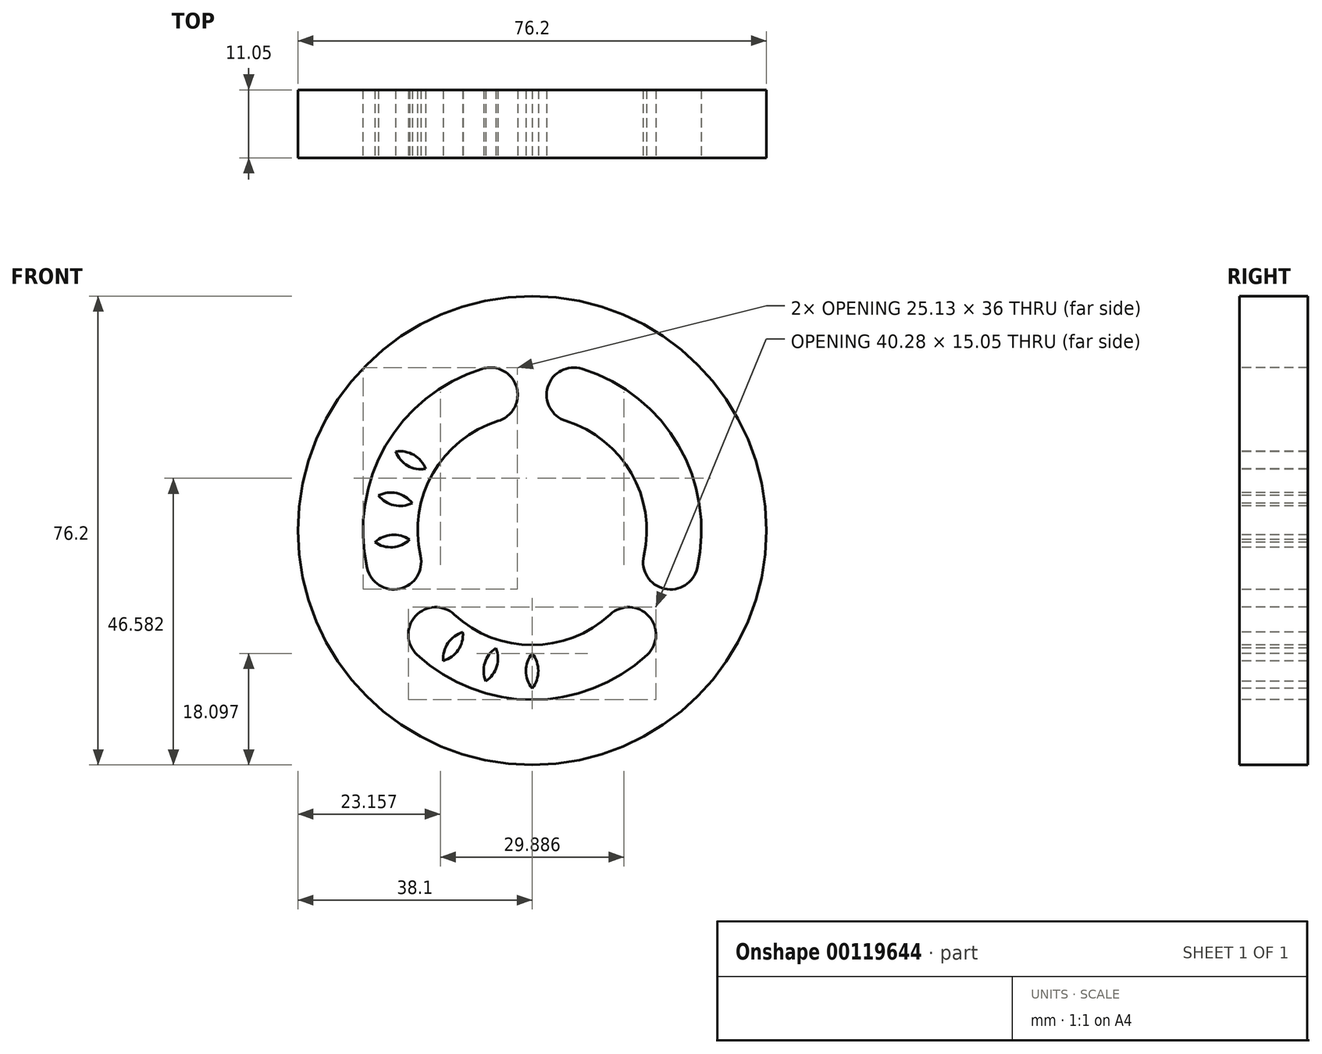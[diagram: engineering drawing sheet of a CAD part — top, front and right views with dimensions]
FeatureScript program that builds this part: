
annotation { "Feature Type Name" : "Feature", "Feature Type Description" : "" }
export const myFeature = defineFeature(function(context is Context, id is Id, definition is map)
    precondition{}
    {
        {
            var Q0;
            Q0=qCreatedBy(makeId("Front.planeOp"),FACE);
            var sketch = newSketch(context, id + "F0", { "sketchPlane" : qUnion([Q0])});
            skCircle(sketch, "E0", {"center": v(0, 0) * mm, "radius": 38.1 * mm});
            skSolve(sketch);
        }
        {
            var Q0;
            Q0 = qSketchRegion(id + "F0", true);
            extrude(context, id + "F1", {"entities" : qUnion([Q0]), "depth" : 11.05 * mm});
        }
        {
            var Q0;
            Q0=makeQuery(id+"F1.opExtrude","CAP_FACE",FACE,{"disambiguationData":[OSD([sQuery(id+"F0.wireOp",EDGE,"E0")])],"isStart":false});
            var sketch = newSketch(context, id + "F2", { "sketchPlane" : qUnion([Q0])});
            skCircle(sketch, "E1", {"center": v(0, 0) * mm, "radius": 7.94 * mm});
            skCircle(sketch, "E2", {"center": v(0, 0) * mm, "radius": 17.46 * mm});
            skCircle(sketch, "E3", {"center": v(0, 0) * mm, "radius": 28.7 * mm});
            skCircle(sketch, "E4", {"center": v(0, 23.08) * mm, "radius": 4.45 * mm, "construction": true});
            skLineSegment(sketch, "E5", {"start": v(0, 17.46) * mm, "end": v(0, 18.64) * mm, "construction": true});
            skLineSegment(sketch, "E6", {"start": v(0, 27.53) * mm, "end": v(0, 28.7) * mm, "construction": true});
            skCircle(sketch, "E7.1.0", {"center": v(-6.8, 22.06) * mm, "radius": 4.45 * mm});
            skCircle(sketch, "E7.2.0", {"center": v(-13, 19.07) * mm, "radius": 4.45 * mm});
            skCircle(sketch, "E7.3.0", {"center": v(-18.05, 14.4) * mm, "radius": 4.45 * mm});
            skCircle(sketch, "E7.4.0", {"center": v(-21.49, 8.43) * mm, "radius": 4.45 * mm});
            skCircle(sketch, "E7.5.0", {"center": v(-23.02, 1.72) * mm, "radius": 4.45 * mm});
            skCircle(sketch, "E7.6.0", {"center": v(-22.5, -5.14) * mm, "radius": 4.45 * mm});
            skCircle(sketch, "E7.7.0", {"center": v(-19.99, -11.54) * mm, "radius": 4.45 * mm, "construction": true});
            skCircle(sketch, "E7.8.0", {"center": v(-15.7, -16.92) * mm, "radius": 4.45 * mm});
            skCircle(sketch, "E7.9.0", {"center": v(-10.02, -20.8) * mm, "radius": 4.45 * mm});
            skCircle(sketch, "E7.10.0", {"center": v(-3.44, -22.82) * mm, "radius": 4.45 * mm});
            skCircle(sketch, "E7.11.0", {"center": v(3.44, -22.82) * mm, "radius": 4.45 * mm});
            skCircle(sketch, "E7.12.0", {"center": v(10.02, -20.8) * mm, "radius": 4.45 * mm});
            skCircle(sketch, "E7.13.0", {"center": v(15.7, -16.92) * mm, "radius": 4.45 * mm});
            skCircle(sketch, "E7.14.0", {"center": v(19.99, -11.54) * mm, "radius": 4.45 * mm, "construction": true});
            skCircle(sketch, "E7.15.0", {"center": v(22.5, -5.14) * mm, "radius": 4.45 * mm});
            skCircle(sketch, "E7.16.0", {"center": v(23.02, 1.72) * mm, "radius": 4.45 * mm});
            skCircle(sketch, "E7.17.0", {"center": v(21.49, 8.43) * mm, "radius": 4.45 * mm});
            skCircle(sketch, "E8.1.18.0", {"center": v(18.05, 14.4) * mm, "radius": 4.45 * mm});
            skCircle(sketch, "E8.1.19.0", {"center": v(13, 19.07) * mm, "radius": 4.45 * mm});
            skCircle(sketch, "E8.1.20.0", {"center": v(6.8, 22.06) * mm, "radius": 4.45 * mm});
            skArc(sketch, "E9", {"start": v(26.84, -6.13) * mm, "mid": v(23.84, 13.76) * mm, "end": v(8.11, 26.3) * mm});
            skArc(sketch, "E10", {"start": v(5.5, 17.8) * mm, "mid": v(16.14, 9.32) * mm, "end": v(18.17, -4.15) * mm});
            skArc(sketch, "E11", {"start": v(18.72, -20.18) * mm, "mid": v(0, -27.53) * mm, "end": v(-18.72, -20.18) * mm});
            skArc(sketch, "E12", {"start": v(-8.11, 26.3) * mm, "mid": v(-23.84, 13.76) * mm, "end": v(-26.84, -6.13) * mm});
            skArc(sketch, "E13", {"start": v(-5.5, 17.8) * mm, "mid": v(-16.14, 9.32) * mm, "end": v(-18.17, -4.15) * mm});
            skArc(sketch, "E14", {"start": v(-12.68, -13.66) * mm, "mid": v(0, -18.64) * mm, "end": v(12.68, -13.66) * mm});
            skSolve(sketch);
        }
        {
            var Q0;
            {var subQ0=sQuery(id+"F2.wireOp",EDGE,"E7.6.0");var subQ1=sQuery(id+"F2.wireOp",EDGE,"E7.5.0");var subQ2=makeQuery(id+"F2.imprint","INTERSECT",VERTEX,{"disambiguationData":[OD(0.0)],"derivedFrom":[subQ1,subQ0]});Q0=makeQuery(id+"F2.imprint","IMPRINT",FACE,{"disambiguationData":[TD([[makeQuery(id+"F2.imprint","IMPRINT",EDGE,{"disambiguationData":[TD([[subQ2,-1.0]])],"derivedFrom":subQ1}),-1.0]])]});}
            var Q1;
            {var subQ0=sQuery(id+"F2.wireOp",EDGE,"E12");var subQ1=sQuery(id+"F2.wireOp",EDGE,"E7.5.0");var subQ2=makeQuery(id+"F2.imprint","INTERSECT",VERTEX,{"derivedFrom":[subQ1,subQ0]});Q1=makeQuery(id+"F2.imprint","IMPRINT",FACE,{"disambiguationData":[TD([[makeQuery(id+"F2.imprint","IMPRINT",EDGE,{"disambiguationData":[TD([[subQ2,-1.0]])],"derivedFrom":subQ1}),-1.0]])]});}
            var Q2;
            {var subQ0=sQuery(id+"F2.wireOp",EDGE,"E7.6.0");var subQ1=sQuery(id+"F2.wireOp",EDGE,"E7.5.0");var subQ2=makeQuery(id+"F2.imprint","INTERSECT",VERTEX,{"disambiguationData":[OD(0.0)],"derivedFrom":[subQ1,subQ0]});Q2=makeQuery(id+"F2.imprint","IMPRINT",FACE,{"disambiguationData":[TD([[makeQuery(id+"F2.imprint","IMPRINT",EDGE,{"disambiguationData":[TD([[subQ2,-1.0]])],"derivedFrom":subQ1}),1.0]])]});}
            var Q3;
            {var subQ0=sQuery(id+"F2.wireOp",EDGE,"E7.6.0");var subQ1=sQuery(id+"F2.wireOp",EDGE,"E7.5.0");var subQ2=makeQuery(id+"F2.imprint","INTERSECT",VERTEX,{"disambiguationData":[OD(1.0)],"derivedFrom":[subQ1,subQ0]});Q3=makeQuery(id+"F2.imprint","IMPRINT",FACE,{"disambiguationData":[TD([[makeQuery(id+"F2.imprint","IMPRINT",EDGE,{"disambiguationData":[TD([[subQ2,-1.0]])],"derivedFrom":subQ1}),-1.0]])]});}
            var Q4;
            {var subQ1=sQuery(id+"F2.wireOp",EDGE,"E7.5.0");var subQ6=sQuery(id+"F2.wireOp",EDGE,"E7.4.0");var subQ7=makeQuery(id+"F2.imprint","INTERSECT",VERTEX,{"disambiguationData":[OD(0.0)],"derivedFrom":[subQ6,subQ1]});Q4=makeQuery(id+"F2.imprint","IMPRINT",FACE,{"disambiguationData":[TD([[makeQuery(id+"F2.imprint","IMPRINT",EDGE,{"disambiguationData":[TD([[subQ7,-1.0]])],"derivedFrom":subQ6}),-1.0]])]});}
            var Q5;
            {var subQ0=sQuery(id+"F2.wireOp",EDGE,"E7.5.0");var subQ1=sQuery(id+"F2.wireOp",EDGE,"E7.4.0");var subQ2=makeQuery(id+"F2.imprint","INTERSECT",VERTEX,{"disambiguationData":[OD(1.0)],"derivedFrom":[subQ1,subQ0]});Q5=makeQuery(id+"F2.imprint","IMPRINT",FACE,{"disambiguationData":[TD([[makeQuery(id+"F2.imprint","IMPRINT",EDGE,{"disambiguationData":[TD([[subQ2,-1.0]])],"derivedFrom":subQ1}),-1.0]])]});}
            var Q6;
            {var subQ0=sQuery(id+"F2.wireOp",EDGE,"E7.4.0");var subQ1=sQuery(id+"F2.wireOp",EDGE,"E7.3.0");var subQ2=makeQuery(id+"F2.imprint","INTERSECT",VERTEX,{"disambiguationData":[OD(1.0)],"derivedFrom":[subQ1,subQ0]});Q6=makeQuery(id+"F2.imprint","IMPRINT",FACE,{"disambiguationData":[TD([[makeQuery(id+"F2.imprint","IMPRINT",EDGE,{"disambiguationData":[TD([[subQ2,-1.0]])],"derivedFrom":subQ1}),-1.0]])]});}
            var Q7;
            {var subQ0=sQuery(id+"F2.wireOp",EDGE,"E7.3.0");var subQ1=sQuery(id+"F2.wireOp",EDGE,"E7.2.0");var subQ2=makeQuery(id+"F2.imprint","INTERSECT",VERTEX,{"disambiguationData":[OD(1.0)],"derivedFrom":[subQ1,subQ0]});Q7=makeQuery(id+"F2.imprint","IMPRINT",FACE,{"disambiguationData":[TD([[makeQuery(id+"F2.imprint","IMPRINT",EDGE,{"disambiguationData":[TD([[subQ2,-1.0]])],"derivedFrom":subQ1}),-1.0]])]});}
            var Q8;
            {var subQ0=sQuery(id+"F2.wireOp",EDGE,"E13");var subQ1=sQuery(id+"F2.wireOp",EDGE,"E7.1.0");var subQ2=makeQuery(id+"F2.imprint","INTERSECT",VERTEX,{"derivedFrom":[subQ1,subQ0]});Q8=makeQuery(id+"F2.imprint","IMPRINT",FACE,{"disambiguationData":[TD([[makeQuery(id+"F2.imprint","IMPRINT",EDGE,{"disambiguationData":[TD([[subQ2,1.0]])],"derivedFrom":subQ1}),-1.0]])]});}
            var Q9;
            {var subQ0=sQuery(id+"F2.wireOp",EDGE,"E7.1.0");var subQ1=makeQuery(id+"F2.imprint","INTERSECT",VERTEX,{"derivedFrom":[subQ0,sQuery(id+"F2.wireOp",EDGE,"E12")]});Q9=makeQuery(id+"F2.imprint","IMPRINT",FACE,{"disambiguationData":[TD([[makeQuery(id+"F2.imprint","IMPRINT",EDGE,{"disambiguationData":[TD([[subQ1,-1.0]])],"derivedFrom":subQ0}),1.0]])]});}
            var Q10;
            {var subQ1=sQuery(id+"F2.wireOp",EDGE,"E7.2.0");var subQ4=sQuery(id+"F2.wireOp",EDGE,"E7.1.0");var subQ5=makeQuery(id+"F2.imprint","INTERSECT",VERTEX,{"disambiguationData":[OD(0.0)],"derivedFrom":[subQ4,subQ1]});Q10=makeQuery(id+"F2.imprint","IMPRINT",FACE,{"disambiguationData":[TD([[makeQuery(id+"F2.imprint","IMPRINT",EDGE,{"disambiguationData":[TD([[subQ5,-1.0]])],"derivedFrom":subQ4}),-1.0]])]});}
            var Q11;
            {var subQ0=sQuery(id+"F2.wireOp",EDGE,"E7.2.0");var subQ1=sQuery(id+"F2.wireOp",EDGE,"E7.1.0");var subQ2=makeQuery(id+"F2.imprint","INTERSECT",VERTEX,{"disambiguationData":[OD(0.0)],"derivedFrom":[subQ1,subQ0]});Q11=makeQuery(id+"F2.imprint","IMPRINT",FACE,{"disambiguationData":[TD([[makeQuery(id+"F2.imprint","IMPRINT",EDGE,{"disambiguationData":[TD([[subQ2,-1.0]])],"derivedFrom":subQ1}),1.0]])]});}
            var Q12;
            {var subQ0=sQuery(id+"F2.wireOp",EDGE,"E12");var subQ1=sQuery(id+"F2.wireOp",EDGE,"E7.1.0");var subQ2=makeQuery(id+"F2.imprint","INTERSECT",VERTEX,{"derivedFrom":[subQ1,subQ0]});Q12=makeQuery(id+"F2.imprint","IMPRINT",FACE,{"disambiguationData":[TD([[makeQuery(id+"F2.imprint","IMPRINT",EDGE,{"disambiguationData":[TD([[subQ2,-1.0]])],"derivedFrom":subQ1}),-1.0]])]});}
            var Q13;
            {var subQ0=sQuery(id+"F2.wireOp",EDGE,"E12");var subQ1=sQuery(id+"F2.wireOp",EDGE,"E7.2.0");var subQ2=makeQuery(id+"F2.imprint","INTERSECT",VERTEX,{"derivedFrom":[subQ1,subQ0]});Q13=makeQuery(id+"F2.imprint","IMPRINT",FACE,{"disambiguationData":[TD([[makeQuery(id+"F2.imprint","IMPRINT",EDGE,{"disambiguationData":[TD([[subQ2,-1.0]])],"derivedFrom":subQ1}),-1.0]])]});}
            var Q14;
            {var subQ0=sQuery(id+"F2.wireOp",EDGE,"E7.3.0");var subQ1=sQuery(id+"F2.wireOp",EDGE,"E7.2.0");var subQ2=makeQuery(id+"F2.imprint","INTERSECT",VERTEX,{"disambiguationData":[OD(0.0)],"derivedFrom":[subQ1,subQ0]});Q14=makeQuery(id+"F2.imprint","IMPRINT",FACE,{"disambiguationData":[TD([[makeQuery(id+"F2.imprint","IMPRINT",EDGE,{"disambiguationData":[TD([[subQ2,-1.0]])],"derivedFrom":subQ1}),1.0]])]});}
            var Q15;
            {var subQ0=sQuery(id+"F2.wireOp",EDGE,"E7.3.0");var subQ4=sQuery(id+"F2.wireOp",EDGE,"E7.2.0");var subQ5=makeQuery(id+"F2.imprint","INTERSECT",VERTEX,{"disambiguationData":[OD(0.0)],"derivedFrom":[subQ4,subQ0]});Q15=makeQuery(id+"F2.imprint","IMPRINT",FACE,{"disambiguationData":[TD([[makeQuery(id+"F2.imprint","IMPRINT",EDGE,{"disambiguationData":[TD([[subQ5,-1.0]])],"derivedFrom":subQ4}),-1.0]])]});}
            var Q16;
            {var subQ0=sQuery(id+"F2.wireOp",EDGE,"E7.4.0");var subQ1=sQuery(id+"F2.wireOp",EDGE,"E7.3.0");var subQ2=makeQuery(id+"F2.imprint","INTERSECT",VERTEX,{"disambiguationData":[OD(0.0)],"derivedFrom":[subQ1,subQ0]});Q16=makeQuery(id+"F2.imprint","IMPRINT",FACE,{"disambiguationData":[TD([[makeQuery(id+"F2.imprint","IMPRINT",EDGE,{"disambiguationData":[TD([[subQ2,-1.0]])],"derivedFrom":subQ1}),-1.0]])]});}
            var Q17;
            {var subQ0=sQuery(id+"F2.wireOp",EDGE,"E7.4.0");var subQ1=sQuery(id+"F2.wireOp",EDGE,"E7.3.0");var subQ2=makeQuery(id+"F2.imprint","INTERSECT",VERTEX,{"disambiguationData":[OD(0.0)],"derivedFrom":[subQ1,subQ0]});Q17=makeQuery(id+"F2.imprint","IMPRINT",FACE,{"disambiguationData":[TD([[makeQuery(id+"F2.imprint","IMPRINT",EDGE,{"disambiguationData":[TD([[subQ2,-1.0]])],"derivedFrom":subQ1}),1.0]])]});}
            var Q18;
            {var subQ0=sQuery(id+"F2.wireOp",EDGE,"E12");var subQ1=sQuery(id+"F2.wireOp",EDGE,"E7.4.0");var subQ2=makeQuery(id+"F2.imprint","INTERSECT",VERTEX,{"derivedFrom":[subQ1,subQ0]});Q18=makeQuery(id+"F2.imprint","IMPRINT",FACE,{"disambiguationData":[TD([[makeQuery(id+"F2.imprint","IMPRINT",EDGE,{"disambiguationData":[TD([[subQ2,-1.0]])],"derivedFrom":subQ1}),-1.0]])]});}
            var Q19;
            {var subQ0=sQuery(id+"F2.wireOp",EDGE,"E7.5.0");var subQ1=sQuery(id+"F2.wireOp",EDGE,"E7.4.0");var subQ2=makeQuery(id+"F2.imprint","INTERSECT",VERTEX,{"disambiguationData":[OD(0.0)],"derivedFrom":[subQ1,subQ0]});Q19=makeQuery(id+"F2.imprint","IMPRINT",FACE,{"disambiguationData":[TD([[makeQuery(id+"F2.imprint","IMPRINT",EDGE,{"disambiguationData":[TD([[subQ2,-1.0]])],"derivedFrom":subQ1}),1.0]])]});}
            var Q20;
            {var subQ0=sQuery(id+"F2.wireOp",EDGE,"E12");var subQ1=sQuery(id+"F2.wireOp",EDGE,"E7.3.0");var subQ2=makeQuery(id+"F2.imprint","INTERSECT",VERTEX,{"derivedFrom":[subQ1,subQ0]});Q20=makeQuery(id+"F2.imprint","IMPRINT",FACE,{"disambiguationData":[TD([[makeQuery(id+"F2.imprint","IMPRINT",EDGE,{"disambiguationData":[TD([[subQ2,-1.0]])],"derivedFrom":subQ1}),-1.0]])]});}
            var Q21;
            {var subQ0=sQuery(id+"F2.wireOp",EDGE,"E8.1.20.0");var subQ1=sQuery(id+"F2.wireOp",EDGE,"E8.1.19.0");var subQ2=makeQuery(id+"F2.imprint","INTERSECT",VERTEX,{"disambiguationData":[OD(0.0)],"derivedFrom":[subQ1,subQ0]});Q21=makeQuery(id+"F2.imprint","IMPRINT",FACE,{"disambiguationData":[TD([[makeQuery(id+"F2.imprint","IMPRINT",EDGE,{"disambiguationData":[TD([[subQ2,-1.0]])],"derivedFrom":subQ1}),-1.0]])]});}
            var Q22;
            {var subQ0=sQuery(id+"F2.wireOp",EDGE,"E9");var subQ1=sQuery(id+"F2.wireOp",EDGE,"E8.1.19.0");var subQ2=makeQuery(id+"F2.imprint","INTERSECT",VERTEX,{"derivedFrom":[subQ1,subQ0]});Q22=makeQuery(id+"F2.imprint","IMPRINT",FACE,{"disambiguationData":[TD([[makeQuery(id+"F2.imprint","IMPRINT",EDGE,{"disambiguationData":[TD([[subQ2,-1.0]])],"derivedFrom":subQ1}),-1.0]])]});}
            var Q23;
            {var subQ1=sQuery(id+"F2.wireOp",EDGE,"E8.1.19.0");var subQ6=sQuery(id+"F2.wireOp",EDGE,"E8.1.18.0");var subQ8=makeQuery(id+"F2.imprint","INTERSECT",VERTEX,{"disambiguationData":[OD(0.0)],"derivedFrom":[subQ6,subQ1]});Q23=makeQuery(id+"F2.imprint","IMPRINT",FACE,{"disambiguationData":[TD([[makeQuery(id+"F2.imprint","IMPRINT",EDGE,{"disambiguationData":[TD([[subQ8,-1.0]])],"derivedFrom":subQ6}),-1.0]])]});}
            var Q24;
            {var subQ0=sQuery(id+"F2.wireOp",EDGE,"E8.1.20.0");var subQ1=sQuery(id+"F2.wireOp",EDGE,"E8.1.19.0");var subQ2=makeQuery(id+"F2.imprint","INTERSECT",VERTEX,{"disambiguationData":[OD(0.0)],"derivedFrom":[subQ1,subQ0]});Q24=makeQuery(id+"F2.imprint","IMPRINT",FACE,{"disambiguationData":[TD([[makeQuery(id+"F2.imprint","IMPRINT",EDGE,{"disambiguationData":[TD([[subQ2,-1.0]])],"derivedFrom":subQ1}),1.0]])]});}
            var Q25;
            {var subQ0=sQuery(id+"F2.wireOp",EDGE,"E8.1.20.0");var subQ1=sQuery(id+"F2.wireOp",EDGE,"E8.1.19.0");var subQ2=makeQuery(id+"F2.imprint","INTERSECT",VERTEX,{"disambiguationData":[OD(1.0)],"derivedFrom":[subQ1,subQ0]});Q25=makeQuery(id+"F2.imprint","IMPRINT",FACE,{"disambiguationData":[TD([[makeQuery(id+"F2.imprint","IMPRINT",EDGE,{"disambiguationData":[TD([[subQ2,-1.0]])],"derivedFrom":subQ1}),-1.0]])]});}
            var Q26;
            {var subQ0=sQuery(id+"F2.wireOp",EDGE,"E9");var subQ1=sQuery(id+"F2.wireOp",EDGE,"E8.1.18.0");var subQ2=makeQuery(id+"F2.imprint","INTERSECT",VERTEX,{"derivedFrom":[subQ1,subQ0]});Q26=makeQuery(id+"F2.imprint","IMPRINT",FACE,{"disambiguationData":[TD([[makeQuery(id+"F2.imprint","IMPRINT",EDGE,{"disambiguationData":[TD([[subQ2,-1.0]])],"derivedFrom":subQ1}),-1.0]])]});}
            var Q27;
            {var subQ0=sQuery(id+"F2.wireOp",EDGE,"E8.1.19.0");var subQ1=sQuery(id+"F2.wireOp",EDGE,"E8.1.18.0");var subQ2=makeQuery(id+"F2.imprint","INTERSECT",VERTEX,{"disambiguationData":[OD(1.0)],"derivedFrom":[subQ1,subQ0]});Q27=makeQuery(id+"F2.imprint","IMPRINT",FACE,{"disambiguationData":[TD([[makeQuery(id+"F2.imprint","IMPRINT",EDGE,{"disambiguationData":[TD([[subQ2,-1.0]])],"derivedFrom":subQ1}),-1.0]])]});}
            var Q28;
            {var subQ0=sQuery(id+"F2.wireOp",EDGE,"E8.1.19.0");var subQ1=sQuery(id+"F2.wireOp",EDGE,"E8.1.18.0");var subQ2=makeQuery(id+"F2.imprint","INTERSECT",VERTEX,{"disambiguationData":[OD(0.0)],"derivedFrom":[subQ1,subQ0]});Q28=makeQuery(id+"F2.imprint","IMPRINT",FACE,{"disambiguationData":[TD([[makeQuery(id+"F2.imprint","IMPRINT",EDGE,{"disambiguationData":[TD([[subQ2,-1.0]])],"derivedFrom":subQ1}),1.0]])]});}
            var Q29;
            {var subQ1=sQuery(id+"F2.wireOp",EDGE,"E8.1.18.0");var subQ4=sQuery(id+"F2.wireOp",EDGE,"E7.17.0");var subQ5=makeQuery(id+"F2.imprint","INTERSECT",VERTEX,{"disambiguationData":[OD(0.0)],"derivedFrom":[subQ4,subQ1]});Q29=makeQuery(id+"F2.imprint","IMPRINT",FACE,{"disambiguationData":[TD([[makeQuery(id+"F2.imprint","IMPRINT",EDGE,{"disambiguationData":[TD([[subQ5,-1.0]])],"derivedFrom":subQ4}),-1.0]])]});}
            var Q30;
            {var subQ0=sQuery(id+"F2.wireOp",EDGE,"E7.17.0");var subQ4=sQuery(id+"F2.wireOp",EDGE,"E7.16.0");var subQ5=makeQuery(id+"F2.imprint","INTERSECT",VERTEX,{"disambiguationData":[OD(0.0)],"derivedFrom":[subQ4,subQ0]});Q30=makeQuery(id+"F2.imprint","IMPRINT",FACE,{"disambiguationData":[TD([[makeQuery(id+"F2.imprint","IMPRINT",EDGE,{"disambiguationData":[TD([[subQ5,-1.0]])],"derivedFrom":subQ4}),-1.0]])]});}
            var Q31;
            {var subQ0=sQuery(id+"F2.wireOp",EDGE,"E9");var subQ1=sQuery(id+"F2.wireOp",EDGE,"E7.17.0");var subQ2=makeQuery(id+"F2.imprint","INTERSECT",VERTEX,{"derivedFrom":[subQ1,subQ0]});Q31=makeQuery(id+"F2.imprint","IMPRINT",FACE,{"disambiguationData":[TD([[makeQuery(id+"F2.imprint","IMPRINT",EDGE,{"disambiguationData":[TD([[subQ2,-1.0]])],"derivedFrom":subQ1}),-1.0]])]});}
            var Q32;
            {var subQ0=sQuery(id+"F2.wireOp",EDGE,"E8.1.18.0");var subQ1=sQuery(id+"F2.wireOp",EDGE,"E7.17.0");var subQ2=makeQuery(id+"F2.imprint","INTERSECT",VERTEX,{"disambiguationData":[OD(0.0)],"derivedFrom":[subQ1,subQ0]});Q32=makeQuery(id+"F2.imprint","IMPRINT",FACE,{"disambiguationData":[TD([[makeQuery(id+"F2.imprint","IMPRINT",EDGE,{"disambiguationData":[TD([[subQ2,-1.0]])],"derivedFrom":subQ1}),1.0]])]});}
            var Q33;
            {var subQ0=sQuery(id+"F2.wireOp",EDGE,"E8.1.18.0");var subQ1=sQuery(id+"F2.wireOp",EDGE,"E7.17.0");var subQ2=makeQuery(id+"F2.imprint","INTERSECT",VERTEX,{"disambiguationData":[OD(1.0)],"derivedFrom":[subQ1,subQ0]});Q33=makeQuery(id+"F2.imprint","IMPRINT",FACE,{"disambiguationData":[TD([[makeQuery(id+"F2.imprint","IMPRINT",EDGE,{"disambiguationData":[TD([[subQ2,-1.0]])],"derivedFrom":subQ1}),-1.0]])]});}
            var Q34;
            {var subQ0=sQuery(id+"F2.wireOp",EDGE,"E9");var subQ1=sQuery(id+"F2.wireOp",EDGE,"E7.16.0");var subQ2=makeQuery(id+"F2.imprint","INTERSECT",VERTEX,{"derivedFrom":[subQ1,subQ0]});Q34=makeQuery(id+"F2.imprint","IMPRINT",FACE,{"disambiguationData":[TD([[makeQuery(id+"F2.imprint","IMPRINT",EDGE,{"disambiguationData":[TD([[subQ2,-1.0]])],"derivedFrom":subQ1}),-1.0]])]});}
            var Q35;
            {var subQ0=sQuery(id+"F2.wireOp",EDGE,"E7.17.0");var subQ1=sQuery(id+"F2.wireOp",EDGE,"E7.16.0");var subQ2=makeQuery(id+"F2.imprint","INTERSECT",VERTEX,{"disambiguationData":[OD(0.0)],"derivedFrom":[subQ1,subQ0]});Q35=makeQuery(id+"F2.imprint","IMPRINT",FACE,{"disambiguationData":[TD([[makeQuery(id+"F2.imprint","IMPRINT",EDGE,{"disambiguationData":[TD([[subQ2,-1.0]])],"derivedFrom":subQ1}),1.0]])]});}
            var Q36;
            {var subQ0=sQuery(id+"F2.wireOp",EDGE,"E7.17.0");var subQ1=sQuery(id+"F2.wireOp",EDGE,"E7.16.0");var subQ2=makeQuery(id+"F2.imprint","INTERSECT",VERTEX,{"disambiguationData":[OD(1.0)],"derivedFrom":[subQ1,subQ0]});Q36=makeQuery(id+"F2.imprint","IMPRINT",FACE,{"disambiguationData":[TD([[makeQuery(id+"F2.imprint","IMPRINT",EDGE,{"disambiguationData":[TD([[subQ2,-1.0]])],"derivedFrom":subQ1}),-1.0]])]});}
            var Q37;
            {var subQ1=sQuery(id+"F2.wireOp",EDGE,"E7.16.0");var subQ4=sQuery(id+"F2.wireOp",EDGE,"E7.15.0");var subQ5=makeQuery(id+"F2.imprint","INTERSECT",VERTEX,{"disambiguationData":[OD(0.0)],"derivedFrom":[subQ4,subQ1]});Q37=makeQuery(id+"F2.imprint","IMPRINT",FACE,{"disambiguationData":[TD([[makeQuery(id+"F2.imprint","IMPRINT",EDGE,{"disambiguationData":[TD([[subQ5,-1.0]])],"derivedFrom":subQ4}),-1.0]])]});}
            var Q38;
            {var subQ0=sQuery(id+"F2.wireOp",EDGE,"E9");var subQ1=sQuery(id+"F2.wireOp",EDGE,"E7.15.0");var subQ2=makeQuery(id+"F2.imprint","INTERSECT",VERTEX,{"derivedFrom":[subQ1,subQ0]});Q38=makeQuery(id+"F2.imprint","IMPRINT",FACE,{"disambiguationData":[TD([[makeQuery(id+"F2.imprint","IMPRINT",EDGE,{"disambiguationData":[TD([[subQ2,-1.0]])],"derivedFrom":subQ1}),-1.0]])]});}
            var Q39;
            {var subQ0=sQuery(id+"F2.wireOp",EDGE,"E7.15.0");var subQ1=makeQuery(id+"F2.imprint","INTERSECT",VERTEX,{"derivedFrom":[subQ0,sQuery(id+"F2.wireOp",EDGE,"E9")]});Q39=makeQuery(id+"F2.imprint","IMPRINT",FACE,{"disambiguationData":[TD([[makeQuery(id+"F2.imprint","IMPRINT",EDGE,{"disambiguationData":[TD([[subQ1,-1.0]])],"derivedFrom":subQ0}),1.0]])]});}
            var Q40;
            {var subQ0=sQuery(id+"F2.wireOp",EDGE,"E7.16.0");var subQ1=sQuery(id+"F2.wireOp",EDGE,"E7.15.0");var subQ2=makeQuery(id+"F2.imprint","INTERSECT",VERTEX,{"disambiguationData":[OD(0.0)],"derivedFrom":[subQ1,subQ0]});Q40=makeQuery(id+"F2.imprint","IMPRINT",FACE,{"disambiguationData":[TD([[makeQuery(id+"F2.imprint","IMPRINT",EDGE,{"disambiguationData":[TD([[subQ2,-1.0]])],"derivedFrom":subQ1}),1.0]])]});}
            var Q41;
            {var subQ0=sQuery(id+"F2.wireOp",EDGE,"E10");var subQ1=sQuery(id+"F2.wireOp",EDGE,"E7.15.0");var subQ2=makeQuery(id+"F2.imprint","INTERSECT",VERTEX,{"derivedFrom":[subQ1,subQ0]});Q41=makeQuery(id+"F2.imprint","IMPRINT",FACE,{"disambiguationData":[TD([[makeQuery(id+"F2.imprint","IMPRINT",EDGE,{"disambiguationData":[TD([[subQ2,1.0]])],"derivedFrom":subQ1}),-1.0]])]});}
            var Q42;
            {var subQ0=sQuery(id+"F2.wireOp",EDGE,"E7.13.0");var subQ1=sQuery(id+"F2.wireOp",EDGE,"E7.12.0");var subQ2=makeQuery(id+"F2.imprint","INTERSECT",VERTEX,{"disambiguationData":[OD(0.0)],"derivedFrom":[subQ1,subQ0]});Q42=makeQuery(id+"F2.imprint","IMPRINT",FACE,{"disambiguationData":[TD([[makeQuery(id+"F2.imprint","IMPRINT",EDGE,{"disambiguationData":[TD([[subQ2,-1.0]])],"derivedFrom":subQ1}),-1.0]])]});}
            var Q43;
            {var subQ0=sQuery(id+"F2.wireOp",EDGE,"E7.13.0");var subQ1=sQuery(id+"F2.wireOp",EDGE,"E7.12.0");var subQ2=makeQuery(id+"F2.imprint","INTERSECT",VERTEX,{"disambiguationData":[OD(1.0)],"derivedFrom":[subQ1,subQ0]});Q43=makeQuery(id+"F2.imprint","IMPRINT",FACE,{"disambiguationData":[TD([[makeQuery(id+"F2.imprint","IMPRINT",EDGE,{"disambiguationData":[TD([[subQ2,-1.0]])],"derivedFrom":subQ1}),-1.0]])]});}
            var Q44;
            {var subQ0=sQuery(id+"F2.wireOp",EDGE,"E7.13.0");var subQ1=sQuery(id+"F2.wireOp",EDGE,"E7.12.0");var subQ2=makeQuery(id+"F2.imprint","INTERSECT",VERTEX,{"disambiguationData":[OD(0.0)],"derivedFrom":[subQ1,subQ0]});Q44=makeQuery(id+"F2.imprint","IMPRINT",FACE,{"disambiguationData":[TD([[makeQuery(id+"F2.imprint","IMPRINT",EDGE,{"disambiguationData":[TD([[subQ2,-1.0]])],"derivedFrom":subQ1}),1.0]])]});}
            var Q45;
            {var subQ0=sQuery(id+"F2.wireOp",EDGE,"E11");var subQ1=sQuery(id+"F2.wireOp",EDGE,"E7.12.0");var subQ2=makeQuery(id+"F2.imprint","INTERSECT",VERTEX,{"derivedFrom":[subQ1,subQ0]});Q45=makeQuery(id+"F2.imprint","IMPRINT",FACE,{"disambiguationData":[TD([[makeQuery(id+"F2.imprint","IMPRINT",EDGE,{"disambiguationData":[TD([[subQ2,-1.0]])],"derivedFrom":subQ1}),-1.0]])]});}
            var Q46;
            {var subQ1=sQuery(id+"F2.wireOp",EDGE,"E7.12.0");var subQ4=sQuery(id+"F2.wireOp",EDGE,"E7.11.0");var subQ5=makeQuery(id+"F2.imprint","INTERSECT",VERTEX,{"disambiguationData":[OD(0.0)],"derivedFrom":[subQ4,subQ1]});Q46=makeQuery(id+"F2.imprint","IMPRINT",FACE,{"disambiguationData":[TD([[makeQuery(id+"F2.imprint","IMPRINT",EDGE,{"disambiguationData":[TD([[subQ5,-1.0]])],"derivedFrom":subQ4}),-1.0]])]});}
            var Q47;
            {var subQ0=sQuery(id+"F2.wireOp",EDGE,"E11");var subQ1=sQuery(id+"F2.wireOp",EDGE,"E7.11.0");var subQ2=makeQuery(id+"F2.imprint","INTERSECT",VERTEX,{"derivedFrom":[subQ1,subQ0]});Q47=makeQuery(id+"F2.imprint","IMPRINT",FACE,{"disambiguationData":[TD([[makeQuery(id+"F2.imprint","IMPRINT",EDGE,{"disambiguationData":[TD([[subQ2,-1.0]])],"derivedFrom":subQ1}),-1.0]])]});}
            var Q48;
            {var subQ0=sQuery(id+"F2.wireOp",EDGE,"E7.12.0");var subQ1=sQuery(id+"F2.wireOp",EDGE,"E7.11.0");var subQ2=makeQuery(id+"F2.imprint","INTERSECT",VERTEX,{"disambiguationData":[OD(1.0)],"derivedFrom":[subQ1,subQ0]});Q48=makeQuery(id+"F2.imprint","IMPRINT",FACE,{"disambiguationData":[TD([[makeQuery(id+"F2.imprint","IMPRINT",EDGE,{"disambiguationData":[TD([[subQ2,-1.0]])],"derivedFrom":subQ1}),-1.0]])]});}
            var Q49;
            {var subQ0=sQuery(id+"F2.wireOp",EDGE,"E7.12.0");var subQ1=sQuery(id+"F2.wireOp",EDGE,"E7.11.0");var subQ2=makeQuery(id+"F2.imprint","INTERSECT",VERTEX,{"disambiguationData":[OD(0.0)],"derivedFrom":[subQ1,subQ0]});Q49=makeQuery(id+"F2.imprint","IMPRINT",FACE,{"disambiguationData":[TD([[makeQuery(id+"F2.imprint","IMPRINT",EDGE,{"disambiguationData":[TD([[subQ2,-1.0]])],"derivedFrom":subQ1}),1.0]])]});}
            var Q50;
            {var subQ1=sQuery(id+"F2.wireOp",EDGE,"E7.11.0");var subQ6=sQuery(id+"F2.wireOp",EDGE,"E7.10.0");var subQ7=makeQuery(id+"F2.imprint","INTERSECT",VERTEX,{"disambiguationData":[OD(0.0)],"derivedFrom":[subQ6,subQ1]});Q50=makeQuery(id+"F2.imprint","IMPRINT",FACE,{"disambiguationData":[TD([[makeQuery(id+"F2.imprint","IMPRINT",EDGE,{"disambiguationData":[TD([[subQ7,-1.0]])],"derivedFrom":subQ6}),-1.0]])]});}
            var Q51;
            {var subQ0=sQuery(id+"F2.wireOp",EDGE,"E11");var subQ1=sQuery(id+"F2.wireOp",EDGE,"E7.10.0");var subQ2=makeQuery(id+"F2.imprint","INTERSECT",VERTEX,{"derivedFrom":[subQ1,subQ0]});Q51=makeQuery(id+"F2.imprint","IMPRINT",FACE,{"disambiguationData":[TD([[makeQuery(id+"F2.imprint","IMPRINT",EDGE,{"disambiguationData":[TD([[subQ2,-1.0]])],"derivedFrom":subQ1}),-1.0]])]});}
            var Q52;
            {var subQ0=sQuery(id+"F2.wireOp",EDGE,"E7.11.0");var subQ1=sQuery(id+"F2.wireOp",EDGE,"E7.10.0");var subQ2=makeQuery(id+"F2.imprint","INTERSECT",VERTEX,{"disambiguationData":[OD(0.0)],"derivedFrom":[subQ1,subQ0]});Q52=makeQuery(id+"F2.imprint","IMPRINT",FACE,{"disambiguationData":[TD([[makeQuery(id+"F2.imprint","IMPRINT",EDGE,{"disambiguationData":[TD([[subQ2,-1.0]])],"derivedFrom":subQ1}),1.0]])]});}
            var Q53;
            {var subQ0=sQuery(id+"F2.wireOp",EDGE,"E7.11.0");var subQ1=sQuery(id+"F2.wireOp",EDGE,"E7.10.0");var subQ2=makeQuery(id+"F2.imprint","INTERSECT",VERTEX,{"disambiguationData":[OD(1.0)],"derivedFrom":[subQ1,subQ0]});Q53=makeQuery(id+"F2.imprint","IMPRINT",FACE,{"disambiguationData":[TD([[makeQuery(id+"F2.imprint","IMPRINT",EDGE,{"disambiguationData":[TD([[subQ2,-1.0]])],"derivedFrom":subQ1}),-1.0]])]});}
            var Q54;
            {var subQ0=sQuery(id+"F2.wireOp",EDGE,"E7.10.0");var subQ4=sQuery(id+"F2.wireOp",EDGE,"E7.9.0");var subQ5=makeQuery(id+"F2.imprint","INTERSECT",VERTEX,{"disambiguationData":[OD(0.0)],"derivedFrom":[subQ4,subQ0]});Q54=makeQuery(id+"F2.imprint","IMPRINT",FACE,{"disambiguationData":[TD([[makeQuery(id+"F2.imprint","IMPRINT",EDGE,{"disambiguationData":[TD([[subQ5,-1.0]])],"derivedFrom":subQ4}),-1.0]])]});}
            var Q55;
            {var subQ0=sQuery(id+"F2.wireOp",EDGE,"E11");var subQ1=sQuery(id+"F2.wireOp",EDGE,"E7.9.0");var subQ2=makeQuery(id+"F2.imprint","INTERSECT",VERTEX,{"derivedFrom":[subQ1,subQ0]});Q55=makeQuery(id+"F2.imprint","IMPRINT",FACE,{"disambiguationData":[TD([[makeQuery(id+"F2.imprint","IMPRINT",EDGE,{"disambiguationData":[TD([[subQ2,-1.0]])],"derivedFrom":subQ1}),-1.0]])]});}
            var Q56;
            {var subQ0=sQuery(id+"F2.wireOp",EDGE,"E7.10.0");var subQ1=sQuery(id+"F2.wireOp",EDGE,"E7.9.0");var subQ2=makeQuery(id+"F2.imprint","INTERSECT",VERTEX,{"disambiguationData":[OD(0.0)],"derivedFrom":[subQ1,subQ0]});Q56=makeQuery(id+"F2.imprint","IMPRINT",FACE,{"disambiguationData":[TD([[makeQuery(id+"F2.imprint","IMPRINT",EDGE,{"disambiguationData":[TD([[subQ2,-1.0]])],"derivedFrom":subQ1}),1.0]])]});}
            var Q57;
            {var subQ0=sQuery(id+"F2.wireOp",EDGE,"E7.10.0");var subQ1=sQuery(id+"F2.wireOp",EDGE,"E7.9.0");var subQ2=makeQuery(id+"F2.imprint","INTERSECT",VERTEX,{"disambiguationData":[OD(1.0)],"derivedFrom":[subQ1,subQ0]});Q57=makeQuery(id+"F2.imprint","IMPRINT",FACE,{"disambiguationData":[TD([[makeQuery(id+"F2.imprint","IMPRINT",EDGE,{"disambiguationData":[TD([[subQ2,-1.0]])],"derivedFrom":subQ1}),-1.0]])]});}
            var Q58;
            {var subQ0=sQuery(id+"F2.wireOp",EDGE,"E7.9.0");var subQ4=sQuery(id+"F2.wireOp",EDGE,"E7.8.0");var subQ5=makeQuery(id+"F2.imprint","INTERSECT",VERTEX,{"disambiguationData":[OD(0.0)],"derivedFrom":[subQ4,subQ0]});Q58=makeQuery(id+"F2.imprint","IMPRINT",FACE,{"disambiguationData":[TD([[makeQuery(id+"F2.imprint","IMPRINT",EDGE,{"disambiguationData":[TD([[subQ5,-1.0]])],"derivedFrom":subQ4}),-1.0]])]});}
            var Q59;
            {var subQ0=sQuery(id+"F2.wireOp",EDGE,"E11");var subQ1=sQuery(id+"F2.wireOp",EDGE,"E7.8.0");var subQ2=makeQuery(id+"F2.imprint","INTERSECT",VERTEX,{"derivedFrom":[subQ1,subQ0]});Q59=makeQuery(id+"F2.imprint","IMPRINT",FACE,{"disambiguationData":[TD([[makeQuery(id+"F2.imprint","IMPRINT",EDGE,{"disambiguationData":[TD([[subQ2,-1.0]])],"derivedFrom":subQ1}),-1.0]])]});}
            var Q60;
            {var subQ0=sQuery(id+"F2.wireOp",EDGE,"E7.9.0");var subQ1=sQuery(id+"F2.wireOp",EDGE,"E7.8.0");var subQ2=makeQuery(id+"F2.imprint","INTERSECT",VERTEX,{"disambiguationData":[OD(0.0)],"derivedFrom":[subQ1,subQ0]});Q60=makeQuery(id+"F2.imprint","IMPRINT",FACE,{"disambiguationData":[TD([[makeQuery(id+"F2.imprint","IMPRINT",EDGE,{"disambiguationData":[TD([[subQ2,-1.0]])],"derivedFrom":subQ1}),1.0]])]});}
            var Q61;
            {var subQ0=sQuery(id+"F2.wireOp",EDGE,"E14");var subQ1=sQuery(id+"F2.wireOp",EDGE,"E7.8.0");var subQ2=makeQuery(id+"F2.imprint","INTERSECT",VERTEX,{"derivedFrom":[subQ1,subQ0]});Q61=makeQuery(id+"F2.imprint","IMPRINT",FACE,{"disambiguationData":[TD([[makeQuery(id+"F2.imprint","IMPRINT",EDGE,{"disambiguationData":[TD([[subQ2,1.0]])],"derivedFrom":subQ1}),-1.0]])]});}
            var Q62;
            {var subQ0=sQuery(id+"F2.wireOp",EDGE,"E7.8.0");var subQ1=makeQuery(id+"F2.imprint","INTERSECT",VERTEX,{"derivedFrom":[subQ0,sQuery(id+"F2.wireOp",EDGE,"E11")]});Q62=makeQuery(id+"F2.imprint","IMPRINT",FACE,{"disambiguationData":[TD([[makeQuery(id+"F2.imprint","IMPRINT",EDGE,{"disambiguationData":[TD([[subQ1,-1.0]])],"derivedFrom":subQ0}),1.0]])]});}
            extrude(context, id + "F3", {"entities" : qUnion([Q0, Q1, Q2, Q3, Q4, Q5, Q6, Q7, Q8, Q9, Q10, Q11, Q12, Q13, Q14, Q15, Q16, Q17, Q18, Q19, Q20, Q21, Q22, Q23, Q24, Q25, Q26, Q27, Q28, Q29, Q30, Q31, Q32, Q33, Q34, Q35, Q36, Q37, Q38, Q39, Q40, Q41, Q42, Q43, Q44, Q45, Q46, Q47, Q48, Q49, Q50, Q51, Q52, Q53, Q54, Q55, Q56, Q57, Q58, Q59, Q60, Q61, Q62]), "operationType" : NewBodyOperationType.REMOVE, "endBound" : BoundingType.THROUGH_ALL, "oppositeDirection" : true, "depth" : 25.4 * mm});
        }
    });
